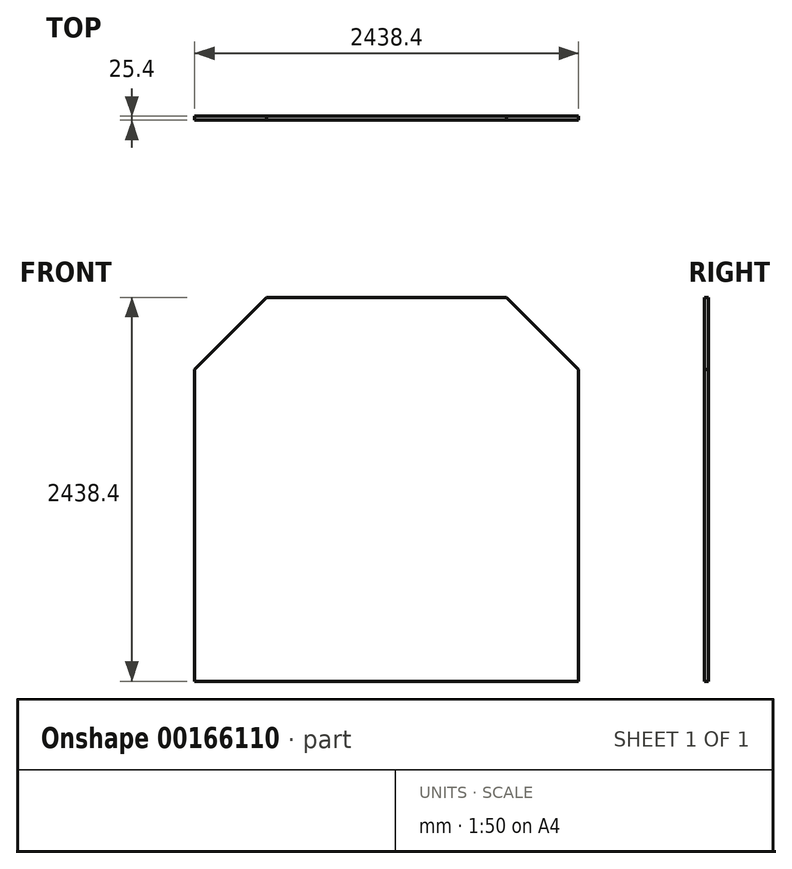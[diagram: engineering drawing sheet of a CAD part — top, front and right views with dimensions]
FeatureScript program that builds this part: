
annotation { "Feature Type Name" : "Feature", "Feature Type Description" : "" }
export const myFeature = defineFeature(function(context is Context, id is Id, definition is map)
    precondition{}
    {
        {
            var Q0;
            Q0=qCreatedBy(makeId("Front.planeOp"),FACE);
            var sketch = newSketch(context, id + "F0", { "sketchPlane" : qUnion([Q0])});
            skLineSegment(sketch, "E0.bottom", {"start": v(0, 0) * mm, "end": v(-1219.2, 0) * mm});
            skLineSegment(sketch, "E0.top", {"start": v(0, 2438.4) * mm, "end": v(-1219.2, 2438.4) * mm});
            skLineSegment(sketch, "E0.left", {"start": v(0, 0) * mm, "end": v(0, 2438.4) * mm});
            skLineSegment(sketch, "E0.right", {"start": v(-1219.2, 0) * mm, "end": v(-1219.2, 2438.4) * mm});
            skLineSegment(sketch, "E1.bottom", {"start": v(0, 0) * mm, "end": v(1219.2, 0) * mm});
            skLineSegment(sketch, "E1.top", {"start": v(0, 2438.4) * mm, "end": v(1219.2, 2438.4) * mm});
            skLineSegment(sketch, "E1.right", {"start": v(1219.2, 0) * mm, "end": v(1219.2, 2438.4) * mm});
            skLineSegment(sketch, "E2", {"start": v(-762, 2438.4) * mm, "end": v(-1219.2, 1981.2) * mm});
            skLineSegment(sketch, "E3", {"start": v(762, 2438.4) * mm, "end": v(1219.2, 1981.2) * mm});
            skSolve(sketch);
        }
        {
            var Q0;
            {var subQ1=sQuery(id+"F0.wireOp",EDGE,"E1.bottom");Q0=makeQuery(id+"F0.imprint","IMPRINT",FACE,{"disambiguationData":[TD([[makeQuery(id+"F0.imprint","IMPRINT",EDGE,{"derivedFrom":subQ1}),1.0]])]});}
            var Q1;
            {var subQ4=sQuery(id+"F0.wireOp",EDGE,"E0.bottom");Q1=makeQuery(id+"F0.imprint","IMPRINT",FACE,{"disambiguationData":[TD([[makeQuery(id+"F0.imprint","IMPRINT",EDGE,{"derivedFrom":subQ4}),-1.0]])]});}
            extrude(context, id + "F1", {"entities" : qUnion([Q0, Q1]), "depth" : 25.4 * mm});
        }
    });
